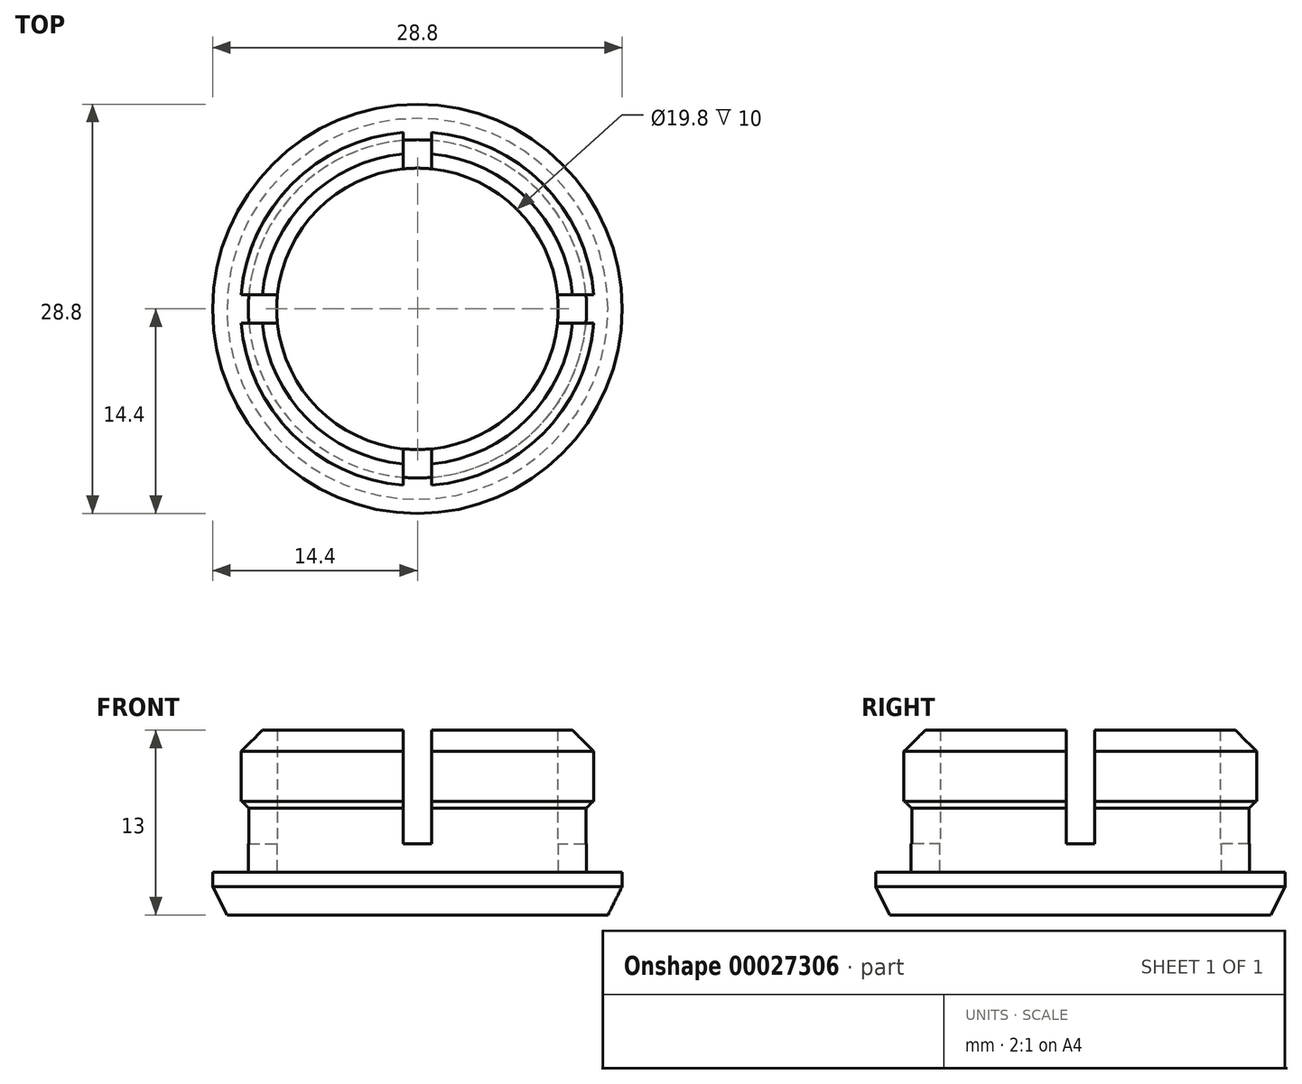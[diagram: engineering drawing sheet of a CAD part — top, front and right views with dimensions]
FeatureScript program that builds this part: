
annotation { "Feature Type Name" : "Feature", "Feature Type Description" : "" }
export const myFeature = defineFeature(function(context is Context, id is Id, definition is map)
    precondition{}
    {
        {
            var Q0;
            Q0=qCreatedBy(makeId("Top.planeOp"),FACE);
            var sketch = newSketch(context, id + "F0", { "sketchPlane" : qUnion([Q0])});
            skCircle(sketch, "E0", {"center": v(0, 0) * mm, "radius": 14.4 * mm});
            skSolve(sketch);
        }
        {
            var Q0;
            Q0 = qSketchRegion(id + "F0", true);
            extrude(context, id + "F1", {"entities" : qUnion([Q0]), "depth" : 3 * mm});
        }
        {
            var Q0;
            Q0=makeQuery(id+"F1.opExtrude","CAP_FACE",FACE,{"disambiguationData":[OSD([sQuery(id+"F0.wireOp",EDGE,"E0")])],"isStart":false});
            var sketch = newSketch(context, id + "F2", { "sketchPlane" : qUnion([Q0])});
            skCircle(sketch, "E1", {"center": v(0, 0) * mm, "radius": 11.9 * mm});
            skCircle(sketch, "E2", {"center": v(0, 0) * mm, "radius": 9.9 * mm});
            skSolve(sketch);
        }
        {
            var Q0;
            Q0 = qSketchRegion(id + "F2", true);
            extrude(context, id + "F3", {"entities" : qUnion([Q0]), "operationType" : NewBodyOperationType.ADD, "depth" : 10 * mm});
        }
        {
            var Q0;
            Q0=makeQuery(id+"F3.opExtrude","CAP_FACE",FACE,{"disambiguationData":[OSD([sQuery(id+"F2.wireOp",EDGE,"E1"),sQuery(id+"F2.wireOp",EDGE,"E2")])],"isStart":false});
            var sketch = newSketch(context, id + "F4", { "sketchPlane" : qUnion([Q0])});
            skCircle(sketch, "E3", {"center": v(0, 0) * mm, "radius": 12.45 * mm});
            skSolve(sketch);
        }
        {
            var Q0;
            Q0=makeQuery(id+"F4.imprint","IMPRINT",FACE,{"disambiguationData":[TD([[makeQuery(id+"F4.imprint","IMPRINT",EDGE,{"derivedFrom":sQuery(id+"F4.wireOp",EDGE,"E3")}),1.0]])]});
            var Q1;
            Q1=makeQuery(id+"F4.imprint","IMPRINT",FACE,{"disambiguationData":[TD([[makeQuery(id+"F4.imprint","IMPRINT",EDGE,{"derivedFrom":makeQuery(id+"F3.opExtrude","CAP_EDGE",EDGE,{"disambiguationData":[OSD([sQuery(id+"F2.wireOp",EDGE,"E2")])],"isStart":false})}),1.0]])]});
            var Q2;
            Q2=makeQuery(id+"F4.imprint","IMPRINT",FACE,{"disambiguationData":[TD([[makeQuery(id+"F4.imprint","IMPRINT",EDGE,{"derivedFrom":makeQuery(id+"F3.opExtrude","CAP_EDGE",EDGE,{"disambiguationData":[OSD([sQuery(id+"F2.wireOp",EDGE,"E1")])],"isStart":false})}),1.0]])]});
            extrude(context, id + "F5", {"entities" : qUnion([Q0, Q1, Q2]), "operationType" : NewBodyOperationType.ADD, "oppositeDirection" : true, "depth" : 5 * mm});
        }
        {
            var Q0;
            Q0=makeQuery(id+"F5.boolean.opBoolean","MERGE",FACE,{"derivedFrom":[makeQuery(id+"F3.opExtrude","CAP_FACE",FACE,{"disambiguationData":[OSD([sQuery(id+"F2.wireOp",EDGE,"E1"),sQuery(id+"F2.wireOp",EDGE,"E2")])],"isStart":false}),makeQuery(id+"F5.opExtrude","CAP_FACE",FACE,{"disambiguationData":[OSD([sQuery(id+"F4.wireOp",EDGE,"E3")])],"isStart":true})]});
            var sketch = newSketch(context, id + "F6", { "sketchPlane" : qUnion([Q0])});
            skCircle(sketch, "E4", {"center": v(0, 0) * mm, "radius": 9.9 * mm});
            skSolve(sketch);
        }
        {
            var Q0;
            Q0 = qSketchRegion(id + "F6", true);
            extrude(context, id + "F7", {"entities" : qUnion([Q0]), "operationType" : NewBodyOperationType.REMOVE, "oppositeDirection" : true, "depth" : 10 * mm});
        }
        {
            var Q0;
            Q0=makeQuery(id+"F3.opExtrude","CAP_FACE",FACE,{"disambiguationData":[OSD([sQuery(id+"F2.wireOp",EDGE,"E1"),sQuery(id+"F2.wireOp",EDGE,"E2")])],"isStart":false});
            var sketch = newSketch(context, id + "F8", { "sketchPlane" : qUnion([Q0])});
            skLineSegment(sketch, "E5.bottom", {"start": v(-1, 15) * mm, "end": v(1, 15) * mm});
            skLineSegment(sketch, "E5.top", {"start": v(-1, -15) * mm, "end": v(1, -15) * mm});
            skLineSegment(sketch, "E5.left", {"start": v(-1, 15) * mm, "end": v(-1, -15) * mm});
            skLineSegment(sketch, "E5.right", {"start": v(1, 15) * mm, "end": v(1, -15) * mm});
            skLineSegment(sketch, "E6.bottom", {"start": v(-15, 1) * mm, "end": v(15, 1) * mm});
            skLineSegment(sketch, "E6.top", {"start": v(-15, -1) * mm, "end": v(15, -1) * mm});
            skLineSegment(sketch, "E6.left", {"start": v(-15, 1) * mm, "end": v(-15, -1) * mm});
            skLineSegment(sketch, "E6.right", {"start": v(15, 1) * mm, "end": v(15, -1) * mm});
            skSolve(sketch);
        }
        {
            var Q0;
            Q0 = qSketchRegion(id + "F8", true);
            extrude(context, id + "F9", {"entities" : qUnion([Q0]), "operationType" : NewBodyOperationType.REMOVE, "oppositeDirection" : true, "depth" : 8 * mm});
        }
        {
            var Q0;
            {var subQ0=sQuery(id+"F4.wireOp",EDGE,"E3");var subQ1=makeQuery(id+"F5.opExtrude","CAP_EDGE",EDGE,{"disambiguationData":[OSD([subQ0])],"isStart":true});var subQ2=sQuery(id+"F8.wireOp",EDGE,"E6.top");var subQ5=sQuery(id+"F8.wireOp",EDGE,"E5.right");var subQ6=makeQuery(id+"F8.imprint","INTERSECT",VERTEX,{"derivedFrom":[subQ5,subQ2]});var subQ9=makeQuery(id+"F8.imprint","INTERSECT",VERTEX,{"disambiguationData":[OD(1.0)],"derivedFrom":[subQ1,subQ5]});Q0=makeQuery(id+"F9.boolean.opBoolean","SPLIT",EDGE,{"disambiguationData":[TD([makeQuery(id+"F9.opExtrude","SWEPT_FACE",FACE,{"disambiguationData":[OSD([subQ5]),TDD([makeQuery(id+"F8.imprint","IMPRINT",EDGE,{"disambiguationData":[TD([[subQ6,-1.0]])],"derivedFrom":subQ5}),makeQuery(id+"F8.imprint","IMPRINT",EDGE,{"disambiguationData":[TD([[subQ9,1.0]])],"derivedFrom":subQ5}),makeQuery(id+"F8.imprint","IMPRINT",EDGE,{"disambiguationData":[TD([[makeQuery(id+"F8.imprint","INTERSECT",VERTEX,{"derivedFrom":[sQuery(id+"F8.wireOp",EDGE,"E5.top"),subQ5]}),1.0]])],"derivedFrom":subQ5})])]})])],"derivedFrom":subQ1});}
            var Q1;
            {var subQ0=sQuery(id+"F4.wireOp",EDGE,"E3");var subQ1=makeQuery(id+"F5.opExtrude","CAP_EDGE",EDGE,{"disambiguationData":[OSD([subQ0])],"isStart":true});var subQ2=sQuery(id+"F8.wireOp",EDGE,"E6.top");var subQ6=sQuery(id+"F8.wireOp",EDGE,"E5.left");var subQ7=makeQuery(id+"F8.imprint","INTERSECT",VERTEX,{"derivedFrom":[subQ6,subQ2]});var subQ9=makeQuery(id+"F8.imprint","INTERSECT",VERTEX,{"disambiguationData":[OD(1.0)],"derivedFrom":[subQ1,subQ6]});Q1=makeQuery(id+"F9.boolean.opBoolean","SPLIT",EDGE,{"disambiguationData":[TD([makeQuery(id+"F9.opExtrude","SWEPT_FACE",FACE,{"disambiguationData":[OSD([subQ6]),TDD([makeQuery(id+"F8.imprint","IMPRINT",EDGE,{"disambiguationData":[TD([[subQ7,-1.0]])],"derivedFrom":subQ6}),makeQuery(id+"F8.imprint","IMPRINT",EDGE,{"disambiguationData":[TD([[subQ9,1.0]])],"derivedFrom":subQ6}),makeQuery(id+"F8.imprint","IMPRINT",EDGE,{"disambiguationData":[TD([[makeQuery(id+"F8.imprint","INTERSECT",VERTEX,{"derivedFrom":[sQuery(id+"F8.wireOp",EDGE,"E5.top"),subQ6]}),1.0]])],"derivedFrom":subQ6})])]})])],"derivedFrom":subQ1});}
            var Q2;
            {var subQ0=sQuery(id+"F4.wireOp",EDGE,"E3");var subQ1=makeQuery(id+"F5.opExtrude","CAP_EDGE",EDGE,{"disambiguationData":[OSD([subQ0])],"isStart":true});var subQ2=sQuery(id+"F8.wireOp",EDGE,"E6.bottom");var subQ6=sQuery(id+"F8.wireOp",EDGE,"E5.left");var subQ7=makeQuery(id+"F8.imprint","INTERSECT",VERTEX,{"derivedFrom":[subQ6,subQ2]});var subQ8=makeQuery(id+"F8.imprint","INTERSECT",VERTEX,{"disambiguationData":[OD(0.0)],"derivedFrom":[subQ1,subQ6]});Q2=makeQuery(id+"F9.boolean.opBoolean","SPLIT",EDGE,{"disambiguationData":[TD([makeQuery(id+"F9.opExtrude","SWEPT_FACE",FACE,{"disambiguationData":[OSD([subQ6]),TDD([makeQuery(id+"F8.imprint","IMPRINT",EDGE,{"disambiguationData":[TD([[makeQuery(id+"F8.imprint","INTERSECT",VERTEX,{"derivedFrom":[sQuery(id+"F8.wireOp",EDGE,"E5.bottom"),subQ6]}),-1.0]])],"derivedFrom":subQ6}),makeQuery(id+"F8.imprint","IMPRINT",EDGE,{"disambiguationData":[TD([[subQ8,-1.0]])],"derivedFrom":subQ6}),makeQuery(id+"F8.imprint","IMPRINT",EDGE,{"disambiguationData":[TD([[subQ7,1.0]])],"derivedFrom":subQ6})])]})])],"derivedFrom":subQ1});}
            var Q3;
            {var subQ0=sQuery(id+"F4.wireOp",EDGE,"E3");var subQ1=makeQuery(id+"F5.opExtrude","CAP_EDGE",EDGE,{"disambiguationData":[OSD([subQ0])],"isStart":true});var subQ2=sQuery(id+"F8.wireOp",EDGE,"E6.bottom");var subQ5=sQuery(id+"F8.wireOp",EDGE,"E5.right");var subQ6=makeQuery(id+"F8.imprint","INTERSECT",VERTEX,{"derivedFrom":[subQ5,subQ2]});var subQ8=makeQuery(id+"F8.imprint","INTERSECT",VERTEX,{"disambiguationData":[OD(0.0)],"derivedFrom":[subQ1,subQ5]});Q3=makeQuery(id+"F9.boolean.opBoolean","SPLIT",EDGE,{"disambiguationData":[TD([makeQuery(id+"F9.opExtrude","SWEPT_FACE",FACE,{"disambiguationData":[OSD([subQ5]),TDD([makeQuery(id+"F8.imprint","IMPRINT",EDGE,{"disambiguationData":[TD([[makeQuery(id+"F8.imprint","INTERSECT",VERTEX,{"derivedFrom":[sQuery(id+"F8.wireOp",EDGE,"E5.bottom"),subQ5]}),-1.0]])],"derivedFrom":subQ5}),makeQuery(id+"F8.imprint","IMPRINT",EDGE,{"disambiguationData":[TD([[subQ8,-1.0]])],"derivedFrom":subQ5}),makeQuery(id+"F8.imprint","IMPRINT",EDGE,{"disambiguationData":[TD([[subQ6,1.0]])],"derivedFrom":subQ5})])]})])],"derivedFrom":subQ1});}
            chamfer(context, id + "F10", {"entities" : qUnion([Q0, Q1, Q2, Q3]), "width" : 1.5 * mm, "tangentPropagation" : true});
        }
        {
            var Q0;
            Q0=makeQuery(id+"F1.opExtrude","CAP_EDGE",EDGE,{"disambiguationData":[OSD([sQuery(id+"F0.wireOp",EDGE,"E0")])],"isStart":true});
            chamfer(context, id + "F11", {"entities" : qUnion([Q0]), "chamferType" : ChamferType.TWO_OFFSETS, "width1" : 2 * mm, "oppositeDirection" : false, "width2" : 1 * mm, "tangentPropagation" : true});
        }
        {
            var Q0;
            {var subQ0=makeQuery(id+"F3.opExtrude","SWEPT_FACE",FACE,{"disambiguationData":[OSD([sQuery(id+"F2.wireOp",EDGE,"E1")])]});var subQ1=sQuery(id+"F4.wireOp",EDGE,"E3");var subQ2=makeQuery(id+"F5.opExtrude","CAP_FACE",FACE,{"disambiguationData":[OSD([subQ1])],"isStart":false});var subQ3=sQuery(id+"F8.wireOp",EDGE,"E6.bottom");var subQ4=makeQuery(id+"F5.opExtrude","CAP_EDGE",EDGE,{"disambiguationData":[OSD([subQ1])],"isStart":true});var subQ8=sQuery(id+"F8.wireOp",EDGE,"E5.left");var subQ9=makeQuery(id+"F8.imprint","INTERSECT",VERTEX,{"derivedFrom":[subQ8,subQ3]});var subQ10=makeQuery(id+"F8.imprint","INTERSECT",VERTEX,{"disambiguationData":[OD(0.0)],"derivedFrom":[subQ4,subQ8]});Q0=makeQuery(id+"F9.boolean.opBoolean","SPLIT",EDGE,{"disambiguationData":[TD([makeQuery(id+"F9.opExtrude","SWEPT_FACE",FACE,{"disambiguationData":[OSD([subQ8]),TDD([makeQuery(id+"F8.imprint","IMPRINT",EDGE,{"disambiguationData":[TD([[makeQuery(id+"F8.imprint","INTERSECT",VERTEX,{"derivedFrom":[sQuery(id+"F8.wireOp",EDGE,"E5.bottom"),subQ8]}),-1.0]])],"derivedFrom":subQ8}),makeQuery(id+"F8.imprint","IMPRINT",EDGE,{"disambiguationData":[TD([[subQ10,-1.0]])],"derivedFrom":subQ8}),makeQuery(id+"F8.imprint","IMPRINT",EDGE,{"disambiguationData":[TD([[subQ9,1.0]])],"derivedFrom":subQ8})])]})])],"derivedFrom":makeQuery(id+"F5.boolean.opBoolean","INTERSECT",EDGE,{"derivedFrom":[subQ0,subQ2]})});}
            var Q1;
            {var subQ0=makeQuery(id+"F3.opExtrude","SWEPT_FACE",FACE,{"disambiguationData":[OSD([sQuery(id+"F2.wireOp",EDGE,"E1")])]});var subQ1=sQuery(id+"F4.wireOp",EDGE,"E3");var subQ2=makeQuery(id+"F5.opExtrude","CAP_FACE",FACE,{"disambiguationData":[OSD([subQ1])],"isStart":false});var subQ3=sQuery(id+"F8.wireOp",EDGE,"E6.bottom");var subQ6=sQuery(id+"F8.wireOp",EDGE,"E5.right");var subQ7=makeQuery(id+"F8.imprint","INTERSECT",VERTEX,{"derivedFrom":[subQ6,subQ3]});var subQ8=makeQuery(id+"F5.opExtrude","CAP_EDGE",EDGE,{"disambiguationData":[OSD([subQ1])],"isStart":true});var subQ10=makeQuery(id+"F8.imprint","INTERSECT",VERTEX,{"disambiguationData":[OD(0.0)],"derivedFrom":[subQ8,subQ6]});Q1=makeQuery(id+"F9.boolean.opBoolean","SPLIT",EDGE,{"disambiguationData":[TD([makeQuery(id+"F9.opExtrude","SWEPT_FACE",FACE,{"disambiguationData":[OSD([subQ6]),TDD([makeQuery(id+"F8.imprint","IMPRINT",EDGE,{"disambiguationData":[TD([[makeQuery(id+"F8.imprint","INTERSECT",VERTEX,{"derivedFrom":[sQuery(id+"F8.wireOp",EDGE,"E5.bottom"),subQ6]}),-1.0]])],"derivedFrom":subQ6}),makeQuery(id+"F8.imprint","IMPRINT",EDGE,{"disambiguationData":[TD([[subQ10,-1.0]])],"derivedFrom":subQ6}),makeQuery(id+"F8.imprint","IMPRINT",EDGE,{"disambiguationData":[TD([[subQ7,1.0]])],"derivedFrom":subQ6})])]})])],"derivedFrom":makeQuery(id+"F5.boolean.opBoolean","INTERSECT",EDGE,{"derivedFrom":[subQ0,subQ2]})});}
            var Q2;
            {var subQ0=makeQuery(id+"F3.opExtrude","SWEPT_FACE",FACE,{"disambiguationData":[OSD([sQuery(id+"F2.wireOp",EDGE,"E1")])]});var subQ1=sQuery(id+"F4.wireOp",EDGE,"E3");var subQ2=makeQuery(id+"F5.opExtrude","CAP_FACE",FACE,{"disambiguationData":[OSD([subQ1])],"isStart":false});var subQ3=sQuery(id+"F8.wireOp",EDGE,"E6.top");var subQ4=makeQuery(id+"F5.opExtrude","CAP_EDGE",EDGE,{"disambiguationData":[OSD([subQ1])],"isStart":true});var subQ8=sQuery(id+"F8.wireOp",EDGE,"E5.left");var subQ9=makeQuery(id+"F8.imprint","INTERSECT",VERTEX,{"derivedFrom":[subQ8,subQ3]});var subQ11=makeQuery(id+"F8.imprint","INTERSECT",VERTEX,{"disambiguationData":[OD(1.0)],"derivedFrom":[subQ4,subQ8]});Q2=makeQuery(id+"F9.boolean.opBoolean","SPLIT",EDGE,{"disambiguationData":[TD([makeQuery(id+"F9.opExtrude","SWEPT_FACE",FACE,{"disambiguationData":[OSD([subQ8]),TDD([makeQuery(id+"F8.imprint","IMPRINT",EDGE,{"disambiguationData":[TD([[subQ9,-1.0]])],"derivedFrom":subQ8}),makeQuery(id+"F8.imprint","IMPRINT",EDGE,{"disambiguationData":[TD([[subQ11,1.0]])],"derivedFrom":subQ8}),makeQuery(id+"F8.imprint","IMPRINT",EDGE,{"disambiguationData":[TD([[makeQuery(id+"F8.imprint","INTERSECT",VERTEX,{"derivedFrom":[sQuery(id+"F8.wireOp",EDGE,"E5.top"),subQ8]}),1.0]])],"derivedFrom":subQ8})])]})])],"derivedFrom":makeQuery(id+"F5.boolean.opBoolean","INTERSECT",EDGE,{"derivedFrom":[subQ0,subQ2]})});}
            var Q3;
            {var subQ0=makeQuery(id+"F3.opExtrude","SWEPT_FACE",FACE,{"disambiguationData":[OSD([sQuery(id+"F2.wireOp",EDGE,"E1")])]});var subQ1=sQuery(id+"F4.wireOp",EDGE,"E3");var subQ2=makeQuery(id+"F5.opExtrude","CAP_FACE",FACE,{"disambiguationData":[OSD([subQ1])],"isStart":false});var subQ3=sQuery(id+"F8.wireOp",EDGE,"E6.top");var subQ6=sQuery(id+"F8.wireOp",EDGE,"E5.right");var subQ7=makeQuery(id+"F8.imprint","INTERSECT",VERTEX,{"derivedFrom":[subQ6,subQ3]});var subQ8=makeQuery(id+"F5.opExtrude","CAP_EDGE",EDGE,{"disambiguationData":[OSD([subQ1])],"isStart":true});var subQ11=makeQuery(id+"F8.imprint","INTERSECT",VERTEX,{"disambiguationData":[OD(1.0)],"derivedFrom":[subQ8,subQ6]});Q3=makeQuery(id+"F9.boolean.opBoolean","SPLIT",EDGE,{"disambiguationData":[TD([makeQuery(id+"F9.opExtrude","SWEPT_FACE",FACE,{"disambiguationData":[OSD([subQ6]),TDD([makeQuery(id+"F8.imprint","IMPRINT",EDGE,{"disambiguationData":[TD([[subQ7,-1.0]])],"derivedFrom":subQ6}),makeQuery(id+"F8.imprint","IMPRINT",EDGE,{"disambiguationData":[TD([[subQ11,1.0]])],"derivedFrom":subQ6}),makeQuery(id+"F8.imprint","IMPRINT",EDGE,{"disambiguationData":[TD([[makeQuery(id+"F8.imprint","INTERSECT",VERTEX,{"derivedFrom":[sQuery(id+"F8.wireOp",EDGE,"E5.top"),subQ6]}),1.0]])],"derivedFrom":subQ6})])]})])],"derivedFrom":makeQuery(id+"F5.boolean.opBoolean","INTERSECT",EDGE,{"derivedFrom":[subQ0,subQ2]})});}
            chamfer(context, id + "F12", {"entities" : qUnion([Q0, Q1, Q2, Q3]), "width" : .5 * mm, "tangentPropagation" : true});
        }
    });
